# Revit family: WVA-4-NPT
name_source: partatom
category: Mechanical Equipment
revit_build: Autodesk Revit MEP 2014 (Build: 20140709_2115(x64)
units: mm (PartAtom-declared; Revit-internal decimal feet)

## types (2) — shared parameters
A = 13 1/2"
ApproximateShipmentWeight = 250 lbs
ArrayRadius = 5 7/8"
B = 29"
BottomExtrusionHeight = 3/8"
BottomRevolveHeight = 3 1/8"
C = 15"
CouplingHeight = 4 1/2"
CylindarDia = 9 1/2"
CylinderHalfLength = 6 3/4"
CylinderHeight = 22 5/8"
D = 14 1/2"
Height1 = 1"
Height2 = 1/8"
HookDiameter = 1/4"
HookDistance = 2 5/8"
HookTopDistance = 3/8"
HookWidth = 3/4"
LeftHookDistance = 3/8"
Manufacturer = Wessels Company
MaximumFlow = 255 GPM
MaximumOperatingPressure = 125 PSIG
MaximumOperatingTemperature = 240°F
Model = WVA-4
NumberOfArray = 9
PartNumber = 72080040
PipeConnectorDiameter = 4"
PipeDiameter = 4 1/2"
RevolveRadius = 4 3/4"
RingDistance = 5 5/8"
SideDrainExtrusion = 7/8"
SideFlangeStep1 = 5 3/8"
SideFlangeStep2 = 9"
SideFlangeThickness = 7/8"
SideFlangeThickness1 = 3/8"
Step1Diameter = 3/4"
Step2Diameter = 1 1/2"
Step3Diameter = 2 1/2"
Step4Diameter = 3 3/8"
Step5Diameter = 3"
TopExtrusionDiameter = 1 1/2"
TotalHeight = 4"
URL = http://westank.com

## type names (no varying parameters)
- WVA-4-NPT
- WVA-4

## geometry (parser evidence)
native form markers: Extrusion x3, Revolve x2, Sweep x5
no freeform markers — native parametric forms only
